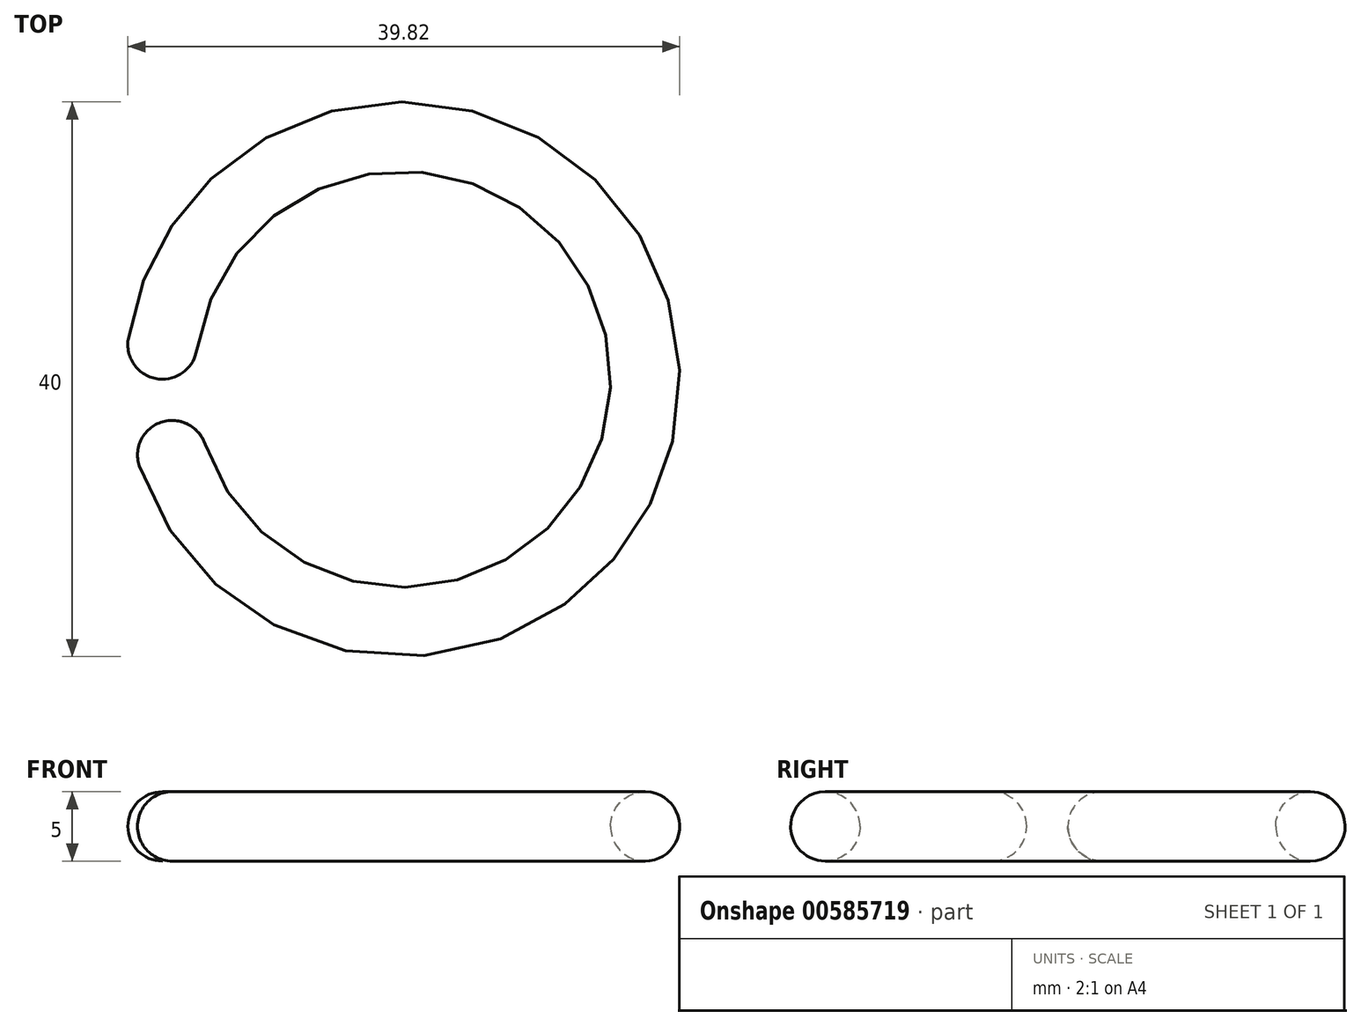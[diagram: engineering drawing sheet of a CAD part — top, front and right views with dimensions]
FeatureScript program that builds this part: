
annotation { "Feature Type Name" : "Feature", "Feature Type Description" : "" }
export const myFeature = defineFeature(function(context is Context, id is Id, definition is map)
    precondition{}
    {
        {
            var Q0;
            Q0=qCreatedBy(makeId("Front.planeOp"),FACE);
            var sketch = newSketch(context, id + "F0", { "sketchPlane" : qUnion([Q0])});
            skLineSegment(sketch, "E0", {"start": v(0, 0) * mm, "end": v(-17.5, 0) * mm, "construction": true});
            skCircle(sketch, "E1", {"center": v(-17.5, 0) * mm, "radius": 2.5 * mm});
            skLineSegment(sketch, "E2", {"start": v(0, 3) * mm, "end": v(0, -3) * mm, "construction": true});
            skSolve(sketch);
        }
        {
            var Q0;
            Q0=makeQuery(id+"F0.imprint","IMPRINT",FACE,{"disambiguationData":[TD([[makeQuery(id+"F0.imprint","IMPRINT",EDGE,{"derivedFrom":sQuery(id+"F0.wireOp",EDGE,"E1")}),1.0]])]});
            var Q1;
            Q1=sQuery(id+"F0.wireOp",EDGE,"E2");
            revolve(context, id + "F1", {"entities" : qUnion([Q0]), "axis" : qUnion([Q1]), "revolveType" : RevolveType.ONE_DIRECTION, "angle" : 350 * degree});
        }
        {
            var Q0;
            Q0=makeQuery(id+"F1.opRevolve","CAP_FACE",FACE,{"disambiguationData":[OSD([sQuery(id+"F0.wireOp",EDGE,"E1")])],"isStart":true});
            var Q1;
            Q1=makeQuery(id+"F1.opRevolve","CAP_FACE",FACE,{"disambiguationData":[OSD([sQuery(id+"F0.wireOp",EDGE,"E1")])],"isStart":false});
            fillet(context, id + "F2", {"entities" : qUnion([Q0, Q1]), "radius" : 2.5 * mm, "tangentPropagation" : true, "allowEdgeOverflow" : false});
        }
    });
